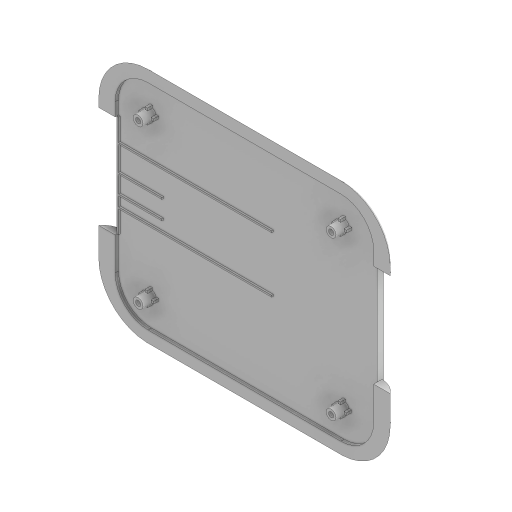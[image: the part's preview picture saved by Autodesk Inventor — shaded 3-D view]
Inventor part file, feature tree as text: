
AUTODESK INVENTOR PART (.ipt)
format: ipt  version: 2024 (Build 280153000, 153)  size: 671,744 bytes
history: native  units: mm
features: extrude x11, fillet x7, sketch x5, hole x1
ambient origin geometry x8: Origin, YZ Plane, XZ Plane, XY Plane, X Axis, Y Axis, Z Axis, Center Point
bodies: Solid1 (feature_tree)
feature tree (24):
  sketch  "Sketch1"  dims[d0=157.0mm d1=130.0mm]
  extrude  "Extrusion1"  Depth=130.0mm
  extrude  "Extrusion2"  Depth=6.0mm
  extrude  "Extrusion4"  Depth=6.0mm
  extrude  "Extrusion5"  Depth=4.0mm
  extrude  "Extrusion6"  Depth=6.0mm
  extrude  "Extrusion7"  Depth=19.9mm
  extrude  "Extrusion8"  Depth=7.0mm
  fillet  "Fillet1"  Radius=6.0mm
  fillet  "Fillet2"  Radius=19.9mm
  extrude  "Extrusion11"  Depth=7.0mm
  fillet  "Fillet4"  Radius=17.0mm
  extrude  "Extrusion12"  Depth=4.0mm
  fillet  "Fillet6"  Radius=4.0mm
  fillet  "Fillet8"  Radius=1.5mm
  fillet  "Fillet9"  Radius=9.0mm
  extrude  "Extrusion13"  Depth=9.0mm
  fillet  "Fillet10"  Radius=1.5mm
  extrude  "Extrusion14"  Depth=1.5mm
  sketch  "Sketch9"  dims[d8=4.0mm d9=6.0mm d10=19.9mm d11=17.0mm d12=6.0mm d13=19.9mm d14=17.0mm d15=17.0mm d16=4.0mm d17=4.0mm d26=1.5mm d27=9.0mm d28=9.0mm d29=1.5mm d30=1.5mm d31=9.0mm d32=1.5mm d33=9.0mm d34=1.5mm d35=9.0mm d36=9.0mm d37=1.5mm d38=9.0mm d39=1.5mm d40=9.0mm d41=1.5mm d42=94.0mm d43=1.0mm d45=27.4mm d46=1.0mm d48=1.0mm d50=1.0mm d51=41.4mm d52=28.0mm d53=10.0mm d54=35.0mm d55=90.0deg d56=177.0mm d57=90.0deg d58=40.0mm d59=47.0mm d60=177.0mm d67=3.0mm d68=0.0mm d69=3.0mm d70=0.0mm d73=1.0mm d74=0.0mm d75=8.0mm d76=0.0mm d77=2.0mm d78=3.0mm d79=0.0mm d80=0.0mm d81=3.0mm d82=0.0mm d83=1.0mm d84=1.0mm d85=3.0mm d86=0.0mm d87=0.0mm d88=20.0mm d89=30.0mm d112=15.0mm d113=13.0mm d114=15.0mm d115=43.5mm d116=43.5mm d117=15.0mm d118=0.0mm d119=12.49998mm d122=0.0mm d123=0.0mm d124=1.0mm d126=1.0mm d127=0.3mm d128=117.2mm d129=96.0mm d130=14.8mm d131=10.3mm d132=5.8mm d133=1.0mm d134=0.0mm d135=19.0mm d136=8.0mm d137=0.0mm d138=4.0mm d139=4.0mm d140=4.0mm d141=4.0mm d142=3.242mm d143=6.0mm d144=4.0mm d145=2.0mm d146=90.0deg d147=7.0mm d148=0.0mm d120=0.0mm d121=0.0mm]
  hole  "Hole1"  [1 undecoded]
  sketch  "Sketch5"  dims[d2=6.0mm d3=17.0mm]
  sketch  "Sketch7"  dims[d4=19.9mm d5=6.0mm]
  sketch  "Sketch8"  dims[d6=19.9mm d7=4.0mm]
note: 1 required parameter value undecoded (feature->parameter linkage not recoverable at this tier; creation-order binding heuristic only, values carry confidence <= 0.55)
